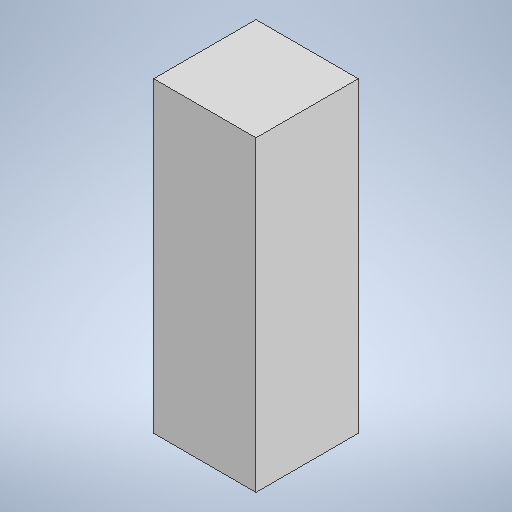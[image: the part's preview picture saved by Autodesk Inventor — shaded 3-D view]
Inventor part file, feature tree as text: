
AUTODESK INVENTOR PART (.ipt)
format: ipt  version: 2025 (Build 290162010, 162A)  size: 255,488 bytes
history: native  units: mm
features: extrude x1, sketch x1
ambient origin geometry x8: Origin, YZ Plane, XZ Plane, XY Plane, X Axis, Y Axis, Z Axis, Center Point
bodies: Solid1 (feature_tree)
feature tree (2):
  extrude  "Extrusion1"  Depth=400.0mm
  sketch  "Sketch1"  dims[d0=400.0mm d1=400.0mm d2=1200.0mm d3=0.0mm]
